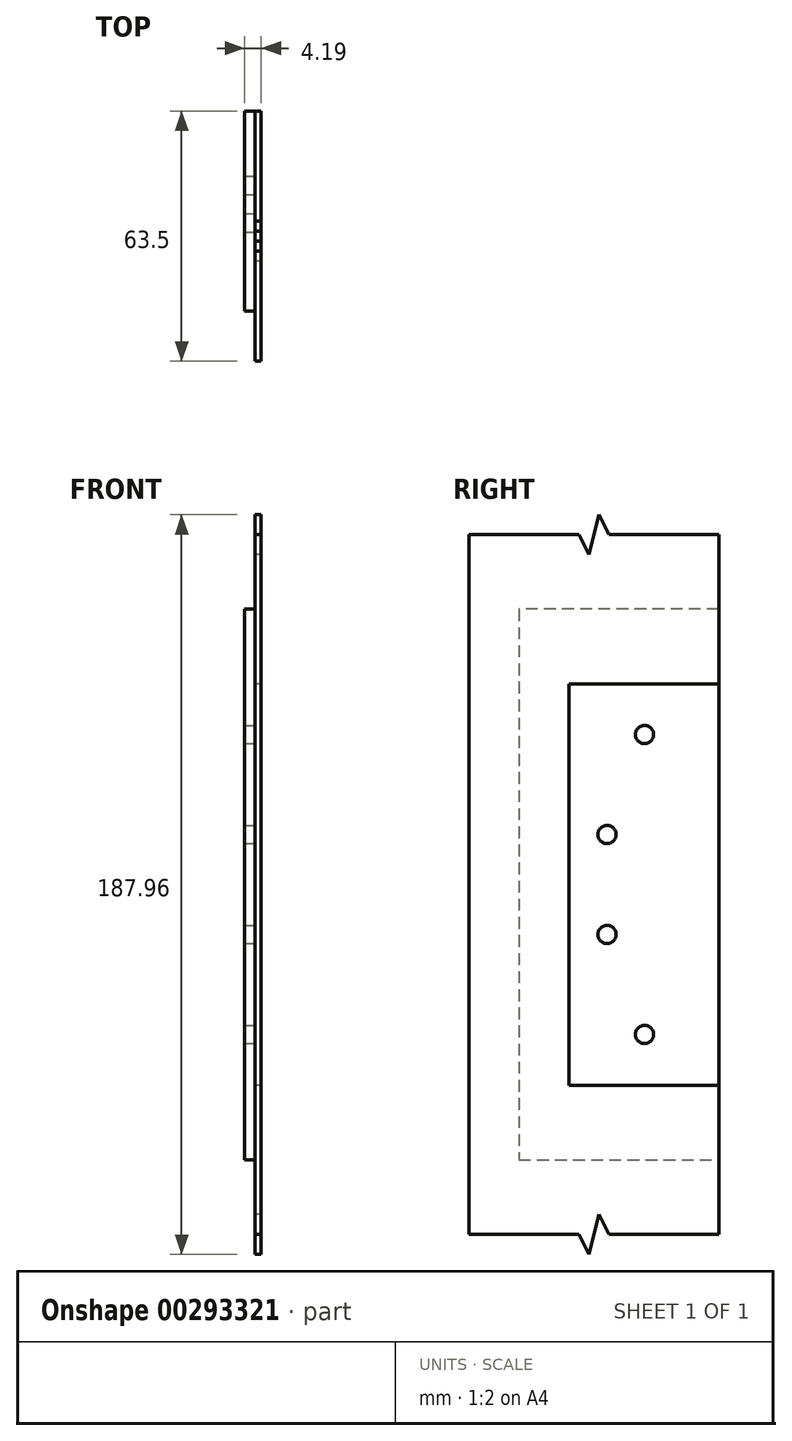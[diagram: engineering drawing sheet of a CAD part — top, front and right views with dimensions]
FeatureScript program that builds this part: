
annotation { "Feature Type Name" : "Feature", "Feature Type Description" : "" }
export const myFeature = defineFeature(function(context is Context, id is Id, definition is map)
    precondition{}
    {
        {
            var Q0;
            Q0=qCreatedBy(makeId("Right.planeOp"),FACE);
            var sketch = newSketch(context, id + "F0", { "sketchPlane" : qUnion([Q0])});
            skLineSegment(sketch, "E0", {"start": v(0, 88.9) * mm, "end": v(-27.94, 88.9) * mm});
            skLineSegment(sketch, "E1", {"start": v(-27.94, 88.9) * mm, "end": v(-30.48, 93.98) * mm});
            skLineSegment(sketch, "E2", {"start": v(-30.48, 93.98) * mm, "end": v(-33.02, 83.82) * mm});
            skLineSegment(sketch, "E3", {"start": v(-33.02, 83.82) * mm, "end": v(-35.56, 88.9) * mm});
            skLineSegment(sketch, "E4", {"start": v(-35.56, 88.9) * mm, "end": v(-63.5, 88.9) * mm});
            skLineSegment(sketch, "E5", {"start": v(-63.5, 88.9) * mm, "end": v(-63.5, -88.9) * mm});
            skLineSegment(sketch, "E6", {"start": v(-63.5, -88.9) * mm, "end": v(-35.56, -88.9) * mm});
            skLineSegment(sketch, "E7", {"start": v(-33.02, -93.98) * mm, "end": v(-35.56, -88.9) * mm});
            skLineSegment(sketch, "E8", {"start": v(-33.02, -93.98) * mm, "end": v(-30.48, -83.82) * mm});
            skLineSegment(sketch, "E9", {"start": v(-30.48, -83.82) * mm, "end": v(-27.94, -88.9) * mm});
            skLineSegment(sketch, "E10", {"start": v(-27.94, -88.9) * mm, "end": v(0, -88.9) * mm});
            skLineSegment(sketch, "E11", {"start": v(0, 88.9) * mm, "end": v(0, 51) * mm});
            skLineSegment(sketch, "E12", {"start": v(0, 51) * mm, "end": v(-38.1, 51) * mm});
            skLineSegment(sketch, "E13", {"start": v(-38.1, 51) * mm, "end": v(-38.1, -51) * mm});
            skLineSegment(sketch, "E14", {"start": v(-38.1, -51) * mm, "end": v(0, -51) * mm});
            skLineSegment(sketch, "E15", {"start": v(0, -51) * mm, "end": v(0, -88.9) * mm});
            skLineSegment(sketch, "E16", {"start": v(0, 51) * mm, "end": v(0, -51) * mm});
            skCircle(sketch, "E17", {"center": v(-28.38, -12.7) * mm, "radius": 2.31 * mm});
            skCircle(sketch, "E18", {"center": v(-18.85, -38.1) * mm, "radius": 2.31 * mm});
            skLineSegment(sketch, "E19", {"start": v(0, 0) * mm, "end": v(-63.5, 0) * mm, "construction": true});
            skCircle(sketch, "E20.MirrorC", {"center": v(-28.38, 12.7) * mm, "radius": 2.31 * mm});
            skCircle(sketch, "E21.MirrorC", {"center": v(-18.85, 38.1) * mm, "radius": 2.31 * mm});
            skLineSegment(sketch, "E22", {"start": v(0, 51) * mm, "end": v(0, 0) * mm, "construction": true});
            skLineSegment(sketch, "E23", {"start": v(0, 0) * mm, "end": v(0, -51) * mm, "construction": true});
            skLineSegment(sketch, "E24", {"start": v(0, 69.95) * mm, "end": v(-50.8, 69.95) * mm});
            skLineSegment(sketch, "E25", {"start": v(-50.8, 69.95) * mm, "end": v(-50.8, -69.95) * mm});
            skPoint(sketch, "E25.endSnap0", {"position": v(0, -69.95) * mm});
            skLineSegment(sketch, "E26", {"start": v(-50.8, -69.95) * mm, "end": v(0, -69.95) * mm});
            skSolve(sketch);
        }
        {
            var Q0;
            Q0=makeQuery(id+"F0.imprint","IMPRINT",FACE,{"disambiguationData":[TD([[makeQuery(id+"F0.imprint","IMPRINT",EDGE,{"derivedFrom":sQuery(id+"F0.wireOp",EDGE,"E0")}),1.0]])]});
            var Q1;
            {var subQ2=sQuery(id+"F0.wireOp",EDGE,"E12");Q1=makeQuery(id+"F0.imprint","IMPRINT",FACE,{"disambiguationData":[TD([[makeQuery(id+"F0.imprint","IMPRINT",EDGE,{"derivedFrom":subQ2}),-1.0]])]});}
            extrude(context, id + "F1", {"entities" : qUnion([Q0, Q1]), "depth" : 1.52 * mm});
        }
        {
            var Q0;
            {var subQ2=sQuery(id+"F0.wireOp",EDGE,"E12");Q0=makeQuery(id+"F0.imprint","IMPRINT",FACE,{"disambiguationData":[TD([[makeQuery(id+"F0.imprint","IMPRINT",EDGE,{"derivedFrom":subQ2}),-1.0]])]});}
            var Q1;
            Q1=makeQuery(id+"F0.imprint","IMPRINT",FACE,{"disambiguationData":[TD([[makeQuery(id+"F0.imprint","IMPRINT",EDGE,{"derivedFrom":sQuery(id+"F0.wireOp",EDGE,"E12")}),1.0]])]});
            extrude(context, id + "F2", {"entities" : qUnion([Q0, Q1]), "operationType" : NewBodyOperationType.ADD, "oppositeDirection" : true, "depth" : 2.67 * mm});
        }
    });
